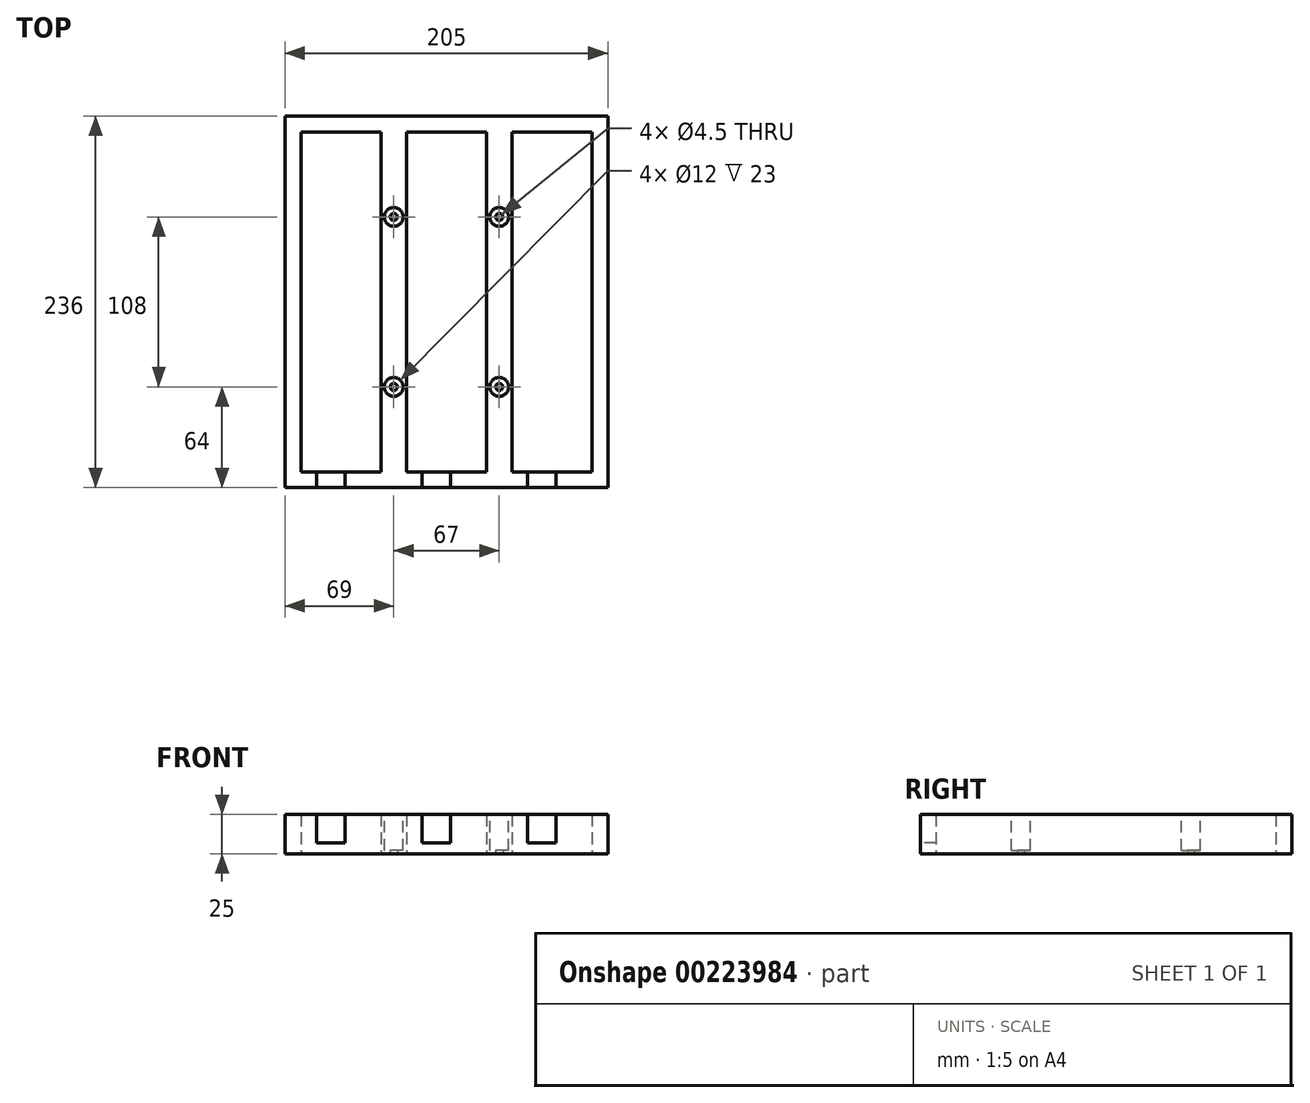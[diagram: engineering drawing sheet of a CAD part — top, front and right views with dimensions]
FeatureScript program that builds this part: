
annotation { "Feature Type Name" : "Feature", "Feature Type Description" : "" }
export const myFeature = defineFeature(function(context is Context, id is Id, definition is map)
    precondition{}
    {
        {
            var Q0;
            Q0=qCreatedBy(makeId("Top.planeOp"),FACE);
            var sketch = newSketch(context, id + "F0", { "sketchPlane" : qUnion([Q0])});
            skLineSegment(sketch, "E0.bottom", {"start": v(-92.5, 108) * mm, "end": v(-41.5, 108) * mm});
            skLineSegment(sketch, "E0.top", {"start": v(-92.5, -108) * mm, "end": v(-41.5, -108) * mm});
            skLineSegment(sketch, "E0.left", {"start": v(-92.5, 108) * mm, "end": v(-92.5, -108) * mm});
            skLineSegment(sketch, "E0.right", {"start": v(-41.5, 108) * mm, "end": v(-41.5, -108) * mm});
            skLineSegment(sketch, "E1.bottom", {"start": v(-25.5, 108) * mm, "end": v(25.5, 108) * mm});
            skLineSegment(sketch, "E1.top", {"start": v(-25.5, -108) * mm, "end": v(25.5, -108) * mm});
            skLineSegment(sketch, "E1.left", {"start": v(-25.5, 108) * mm, "end": v(-25.5, -108) * mm});
            skLineSegment(sketch, "E1.right", {"start": v(25.5, 108) * mm, "end": v(25.5, -108) * mm});
            skLineSegment(sketch, "E2.bottom", {"start": v(41.5, 108) * mm, "end": v(92.5, 108) * mm});
            skLineSegment(sketch, "E2.top", {"start": v(41.5, -108) * mm, "end": v(92.5, -108) * mm});
            skLineSegment(sketch, "E2.left", {"start": v(41.5, 108) * mm, "end": v(41.5, -108) * mm});
            skLineSegment(sketch, "E2.right", {"start": v(92.5, 108) * mm, "end": v(92.5, -108) * mm});
            skLineSegment(sketch, "E3", {"start": v(-41.5, 0) * mm, "end": v(-25.5, 0) * mm, "construction": true});
            skLineSegment(sketch, "E4", {"start": v(25.5, 0) * mm, "end": v(41.5, 0) * mm, "construction": true});
            skLineSegment(sketch, "E5", {"start": v(-25.5, 0) * mm, "end": v(25.5, 0) * mm, "construction": true});
            skPoint(sketch, "E6", {"position": v(0, 0) * mm});
            skLineSegment(sketch, "E7.bottom", {"start": v(-102.5, 118) * mm, "end": v(102.5, 118) * mm});
            skLineSegment(sketch, "E7.top", {"start": v(-102.5, -118) * mm, "end": v(102.5, -118) * mm});
            skLineSegment(sketch, "E7.left", {"start": v(-102.5, 118) * mm, "end": v(-102.5, -118) * mm});
            skLineSegment(sketch, "E7.right", {"start": v(102.5, 118) * mm, "end": v(102.5, -118) * mm});
            skLineSegment(sketch, "E8", {"start": v(0, 108) * mm, "end": v(0, 118) * mm, "construction": true});
            skLineSegment(sketch, "E9", {"start": v(92.5, 0) * mm, "end": v(102.5, 0) * mm, "construction": true});
            skLineSegment(sketch, "E10", {"start": v(0, -108) * mm, "end": v(0, -118) * mm, "construction": true});
            skLineSegment(sketch, "E11", {"start": v(-92.5, 0) * mm, "end": v(-102.5, 0) * mm, "construction": true});
            skPoint(sketch, "E12", {"position": v(-33.5, 0) * mm});
            skLineSegment(sketch, "E13", {"start": v(-33.5, 54) * mm, "end": v(-33.5, -54) * mm, "construction": true});
            skCircle(sketch, "E14", {"center": v(-33.5, 54) * mm, "radius": 2.25 * mm});
            skCircle(sketch, "E15", {"center": v(-33.5, -54) * mm, "radius": 2.25 * mm});
            skCircle(sketch, "E16.MirrorC", {"center": v(33.5, 54) * mm, "radius": 2.25 * mm});
            skCircle(sketch, "E17.MirrorC", {"center": v(33.5, -54) * mm, "radius": 2.25 * mm});
            skSolve(sketch);
        }
        {
            var Q0;
            Q0 = qSketchRegion(id + "F0", true);
            extrude(context, id + "F1", {"entities" : qUnion([Q0]), "depth" : 25 * mm});
        }
        {
            var Q0;
            Q0=makeQuery(id+"F1.opExtrude","SWEPT_FACE",FACE,{"disambiguationData":[OSD([sQuery(id+"F0.wireOp",EDGE,"E7.top")])]});
            var sketch = newSketch(context, id + "F2", { "sketchPlane" : qUnion([Q0])});
            skLineSegment(sketch, "E18.0", {"start": v(-92.5, 25) * mm, "end": v(-92.5, 0) * mm, "construction": true});
            skLineSegment(sketch, "E18.1", {"start": v(-25.5, 25) * mm, "end": v(-25.5, 0) * mm, "construction": true});
            skLineSegment(sketch, "E18.2", {"start": v(41.5, 25) * mm, "end": v(41.5, 0) * mm, "construction": true});
            skLineSegment(sketch, "E19.bottom", {"start": v(-82.5, 25) * mm, "end": v(-64.5, 25) * mm});
            skLineSegment(sketch, "E19.top", {"start": v(-82.5, 7) * mm, "end": v(-64.5, 7) * mm});
            skLineSegment(sketch, "E19.left", {"start": v(-82.5, 25) * mm, "end": v(-82.5, 7) * mm});
            skLineSegment(sketch, "E19.right", {"start": v(-64.5, 25) * mm, "end": v(-64.5, 7) * mm});
            skLineSegment(sketch, "E20.bottom", {"start": v(-15.5, 25) * mm, "end": v(2.5, 25) * mm});
            skLineSegment(sketch, "E20.top", {"start": v(-15.5, 7) * mm, "end": v(2.5, 7) * mm});
            skLineSegment(sketch, "E20.left", {"start": v(-15.5, 25) * mm, "end": v(-15.5, 7) * mm});
            skLineSegment(sketch, "E20.right", {"start": v(2.5, 25) * mm, "end": v(2.5, 7) * mm});
            skLineSegment(sketch, "E21.bottom", {"start": v(51.5, 25) * mm, "end": v(69.5, 25) * mm});
            skLineSegment(sketch, "E21.top", {"start": v(51.5, 7) * mm, "end": v(69.5, 7) * mm});
            skLineSegment(sketch, "E21.left", {"start": v(51.5, 25) * mm, "end": v(51.5, 7) * mm});
            skLineSegment(sketch, "E21.right", {"start": v(69.5, 25) * mm, "end": v(69.5, 7) * mm});
            skLineSegment(sketch, "E22", {"start": v(-82.5, 16) * mm, "end": v(-92.5, 16) * mm, "construction": true});
            skLineSegment(sketch, "E23", {"start": v(-15.5, 16) * mm, "end": v(-25.5, 16) * mm, "construction": true});
            skLineSegment(sketch, "E24", {"start": v(51.5, 16) * mm, "end": v(41.5, 16) * mm, "construction": true});
            skSolve(sketch);
        }
        {
            var Q0;
            Q0 = qSketchRegion(id + "F2", true);
            var Q1;
            Q1=makeQuery(id+"F1.opExtrude","SWEPT_FACE",FACE,{"disambiguationData":[OSD([sQuery(id+"F0.wireOp",EDGE,"E0.top")])]});
            extrude(context, id + "F3", {"entities" : qUnion([Q0]), "operationType" : NewBodyOperationType.REMOVE, "endBound" : BoundingType.UP_TO_SURFACE, "oppositeDirection" : true, "endBoundEntityFace" : qUnion([Q1]), "depth" : 25 * mm});
        }
        {
            var Q0;
            Q0=makeQuery(id+"F1.opExtrude","CAP_FACE",FACE,{"disambiguationData":[OSD([sQuery(id+"F0.wireOp",EDGE,"E0.bottom"),sQuery(id+"F0.wireOp",EDGE,"E0.top"),sQuery(id+"F0.wireOp",EDGE,"E0.left"),sQuery(id+"F0.wireOp",EDGE,"E0.right"),sQuery(id+"F0.wireOp",EDGE,"E1.bottom"),sQuery(id+"F0.wireOp",EDGE,"E1.top"),sQuery(id+"F0.wireOp",EDGE,"E1.left"),sQuery(id+"F0.wireOp",EDGE,"E1.right"),sQuery(id+"F0.wireOp",EDGE,"E2.bottom"),sQuery(id+"F0.wireOp",EDGE,"E2.top"),sQuery(id+"F0.wireOp",EDGE,"E2.left"),sQuery(id+"F0.wireOp",EDGE,"E2.right"),sQuery(id+"F0.wireOp",EDGE,"E7.bottom"),sQuery(id+"F0.wireOp",EDGE,"E7.top"),sQuery(id+"F0.wireOp",EDGE,"E7.left"),sQuery(id+"F0.wireOp",EDGE,"E7.right"),sQuery(id+"F0.wireOp",EDGE,"E14"),sQuery(id+"F0.wireOp",EDGE,"E15"),sQuery(id+"F0.wireOp",EDGE,"E16.MirrorC"),sQuery(id+"F0.wireOp",EDGE,"E17.MirrorC")])],"isStart":false});
            var sketch = newSketch(context, id + "F4", { "sketchPlane" : qUnion([Q0])});
            skCircle(sketch, "E25", {"center": v(-33.5, 54) * mm, "radius": 6 * mm});
            skCircle(sketch, "E26", {"center": v(-33.5, -54) * mm, "radius": 6 * mm});
            skCircle(sketch, "E27.MirrorC", {"center": v(33.5, 54) * mm, "radius": 6 * mm});
            skCircle(sketch, "E28.MirrorC", {"center": v(33.5, -54) * mm, "radius": 6 * mm});
            skSolve(sketch);
        }
        {
            var Q0;
            Q0 = qSketchRegion(id + "F4", true);
            extrude(context, id + "F5", {"entities" : qUnion([Q0]), "operationType" : NewBodyOperationType.REMOVE, "oppositeDirection" : true, "depth" : 23 * mm});
        }
    });
